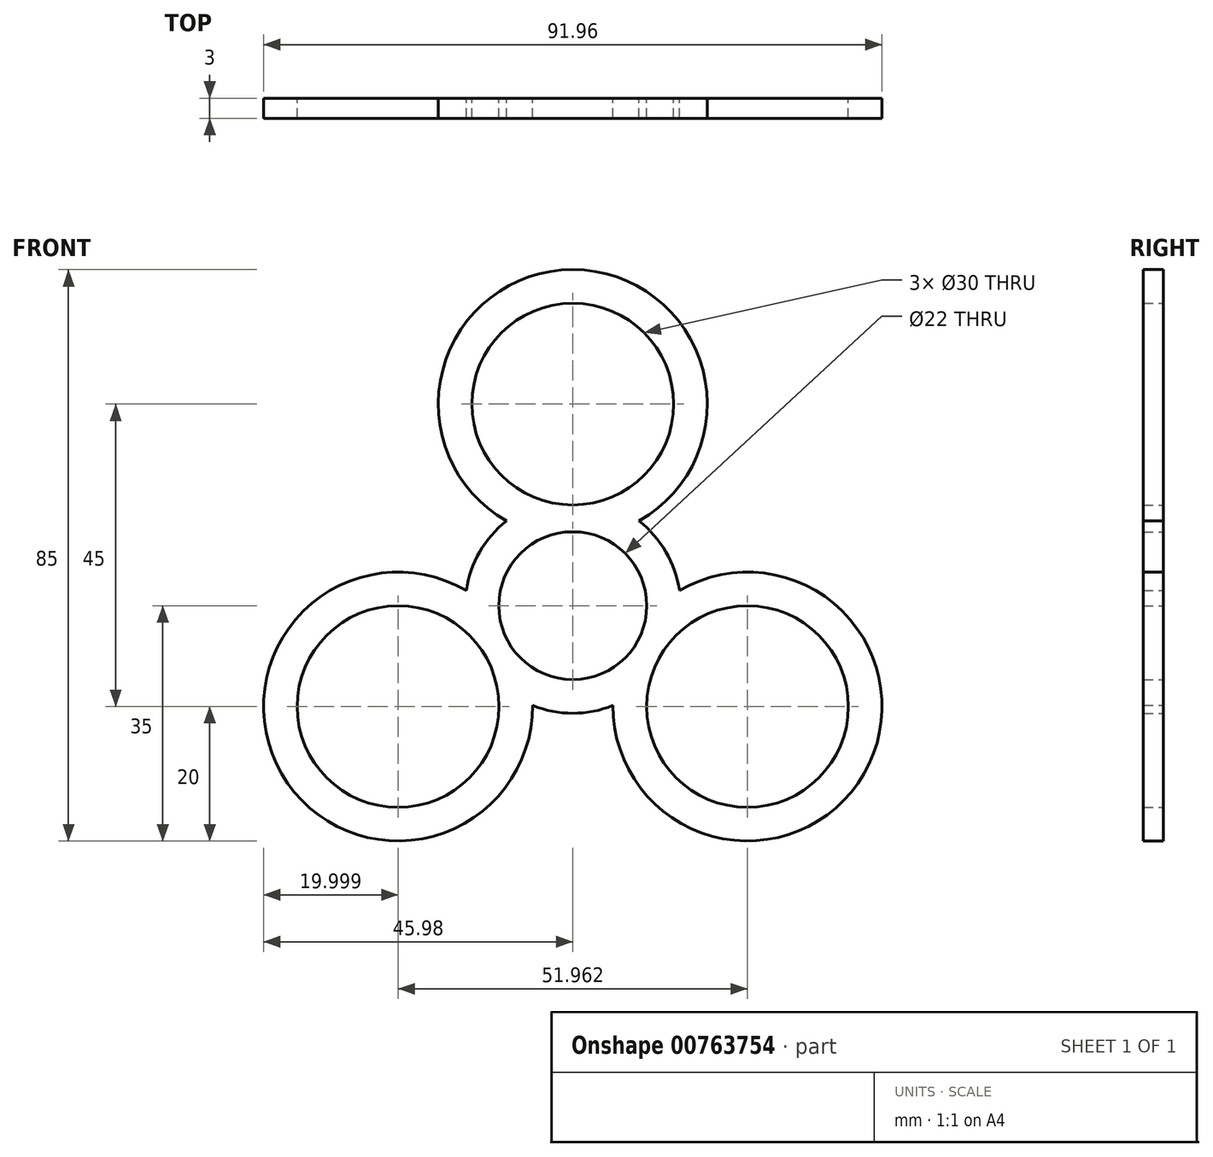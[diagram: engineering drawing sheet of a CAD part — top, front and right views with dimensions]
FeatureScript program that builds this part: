
annotation { "Feature Type Name" : "Feature", "Feature Type Description" : "" }
export const myFeature = defineFeature(function(context is Context, id is Id, definition is map)
    precondition{}
    {
        {
            var Q0;
            Q0=qCreatedBy(makeId("Front.planeOp"),FACE);
            var sketch = newSketch(context, id + "F0", { "sketchPlane" : qUnion([Q0])});
            skCircle(sketch, "E0", {"center": v(0, 30) * mm, "radius": 15 * mm});
            skArc(sketch, "E1", {"start": v(9.86, 12.6) * mm, "mid": v(0, 50) * mm, "end": v(-9.86, 12.6) * mm});
            skArc(sketch, "E2", {"start": v(-9.86, 12.6) * mm, "mid": v(-12.08, 10.5) * mm, "end": v(-13.86, 8) * mm});
            skArc(sketch, "E3.trimOffspring", {"start": v(13.86, 8) * mm, "mid": v(12.08, 10.5) * mm, "end": v(9.86, 12.6) * mm});
            skArc(sketch, "E4", {"start": v(9.53, 5.5) * mm, "mid": v(0, 11) * mm, "end": v(-9.53, 5.5) * mm});
            skArc(sketch, "E5.1.0", {"start": v(-15.84, 2.24) * mm, "mid": v(-43.3, -25) * mm, "end": v(-5.98, -14.84) * mm});
            skCircle(sketch, "E5.1.1", {"center": v(-25.98, -15) * mm, "radius": 15 * mm});
            skArc(sketch, "E5.1.2", {"start": v(-9.53, 5.5) * mm, "mid": v(-9.53, -5.5) * mm, "end": v(0, -11) * mm});
            skArc(sketch, "E5.1.3", {"start": v(-5.98, -14.84) * mm, "mid": v(-3.05, -15.7) * mm, "end": v(0, -16) * mm});
            skArc(sketch, "E5.1.4", {"start": v(-13.86, 8) * mm, "mid": v(-15.13, 5.22) * mm, "end": v(-15.84, 2.24) * mm});
            skArc(sketch, "E5.2.0", {"start": v(5.98, -14.84) * mm, "mid": v(43.3, -25) * mm, "end": v(15.84, 2.24) * mm});
            skCircle(sketch, "E5.2.1", {"center": v(25.98, -15) * mm, "radius": 15 * mm});
            skArc(sketch, "E5.2.2", {"start": v(0, -11) * mm, "mid": v(9.53, -5.5) * mm, "end": v(9.53, 5.5) * mm});
            skArc(sketch, "E5.2.3", {"start": v(15.84, 2.24) * mm, "mid": v(15.13, 5.22) * mm, "end": v(13.86, 8) * mm});
            skArc(sketch, "E5.2.4", {"start": v(0, -16) * mm, "mid": v(3.05, -15.7) * mm, "end": v(5.98, -14.84) * mm});
            skSolve(sketch);
        }
        {
            var Q0;
            Q0=makeQuery(id+"F0.imprint","IMPRINT",FACE,{"disambiguationData":[TD([[makeQuery(id+"F0.imprint","IMPRINT",EDGE,{"derivedFrom":sQuery(id+"F0.wireOp",EDGE,"E0")}),-1.0]])]});
            extrude(context, id + "F1", {"entities" : qUnion([Q0]), "depth" : 3 * mm, "offsetDistance" : 25 * mm});
        }
    });
